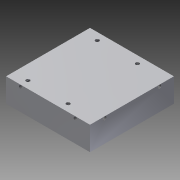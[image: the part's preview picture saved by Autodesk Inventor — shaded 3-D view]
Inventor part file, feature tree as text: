
AUTODESK INVENTOR PART (.ipt)
format: ipt  version: 2013 (Build 170138000, 138)  size: 160,768 bytes
history: native  units: mm
features: thread x12, sketch x5, hole x3, extrude x2, other x1
ambient origin geometry x1: Origin
feature tree (23):
  other  "ソリッド1"
  extrude  "押し出し1"  Depth=46.0mm
  hole  "穴1"  [1 undecoded]
  hole  "穴2"  [1 undecoded]
  hole  "穴3"  [1 undecoded]
  thread  "ねじ1"
  thread  "ねじ3"
  thread  "ねじ5"
  thread  "ねじ6"
  thread  "ねじ11"
  thread  "ねじ13"
  thread  "ねじ14"
  thread  "ねじ16"
  thread  "ねじ17"
  thread  "ねじ18"
  thread  "ねじ19"
  thread  "ねじ20"
  extrude  "押し出し2"  Depth=15.0mm TaperAngle=0.0deg
  sketch  "スケッチ1"
  sketch  "スケッチ2"
  sketch  "スケッチ3"
  sketch  "スケッチ4"
  sketch  "スケッチ5"
note: 3 required parameter values undecoded (feature->parameter linkage not recoverable at this tier; creation-order binding heuristic only, values carry confidence <= 0.55)
